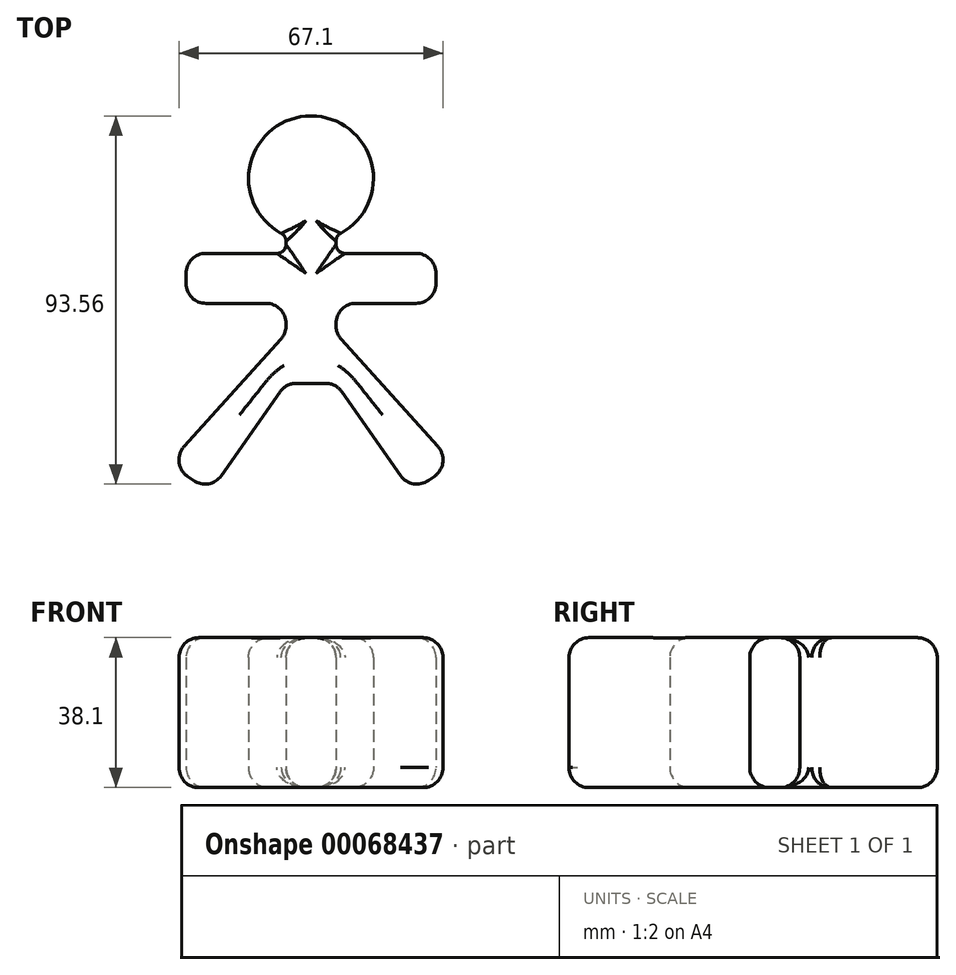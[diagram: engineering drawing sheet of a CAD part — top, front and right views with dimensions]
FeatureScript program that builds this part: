
annotation { "Feature Type Name" : "Feature", "Feature Type Description" : "" }
export const myFeature = defineFeature(function(context is Context, id is Id, definition is map)
    precondition{}
    {
        {
            var Q0;
            Q0=qCreatedBy(makeId("Top.planeOp"),FACE);
            var sketch = newSketch(context, id + "F0", { "sketchPlane" : qUnion([Q0])});
            skLineSegment(sketch, "E0.bottom", {"start": v(0, 0) * mm, "end": v(12.7, 0) * mm});
            skLineSegment(sketch, "E0.top", {"start": v(0, 38.1) * mm, "end": v(12.7, 38.1) * mm});
            skLineSegment(sketch, "E0.left", {"start": v(0, 0) * mm, "end": v(0, 38.1) * mm});
            skLineSegment(sketch, "E0.right", {"start": v(12.7, 0) * mm, "end": v(12.7, 38.1) * mm});
            skLineSegment(sketch, "E1.bottom", {"start": v(-25.4, 33.02) * mm, "end": v(38.1, 33.02) * mm});
            skLineSegment(sketch, "E1.top", {"start": v(-25.4, 20.32) * mm, "end": v(38.1, 20.32) * mm});
            skLineSegment(sketch, "E1.left", {"start": v(-25.4, 33.02) * mm, "end": v(-25.4, 20.32) * mm});
            skLineSegment(sketch, "E1.right", {"start": v(38.1, 33.02) * mm, "end": v(38.1, 20.32) * mm});
            skLineSegment(sketch, "E2.top", {"start": v(-19.33, -27.6) * mm, "end": v(-29.73, -20.32) * mm});
            skLineSegment(sketch, "E2.left", {"start": v(0, 0) * mm, "end": v(-19.33, -27.6) * mm});
            skLineSegment(sketch, "E2.right", {"start": v(0, 12.7) * mm, "end": v(-29.73, -20.32) * mm});
            skLineSegment(sketch, "E3.top", {"start": v(32.03, -27.6) * mm, "end": v(42.43, -20.32) * mm});
            skLineSegment(sketch, "E3.left", {"start": v(12.7, 0) * mm, "end": v(32.03, -27.6) * mm});
            skLineSegment(sketch, "E3.right", {"start": v(12.7, 12.7) * mm, "end": v(42.43, -20.32) * mm});
            skCircle(sketch, "E4", {"center": v(6.35, 52.07) * mm, "radius": 15.88 * mm});
            skSolve(sketch);
        }
        {
            var Q0;
            Q0 = qSketchRegion(id + "F0", true);
            extrude(context, id + "F1", {"entities" : qUnion([Q0]), "depth" : 38.1 * mm});
        }
        {
            var Q0;
            Q0=makeQuery(id+"F1.opExtrude","CAP_FACE",FACE,{"disambiguationData":[OSD([sQuery(id+"F0.wireOp",EDGE,"E0.bottom"),sQuery(id+"F0.wireOp",EDGE,"E0.left"),sQuery(id+"F0.wireOp",EDGE,"E0.right"),sQuery(id+"F0.wireOp",EDGE,"E1.bottom"),sQuery(id+"F0.wireOp",EDGE,"E1.top"),sQuery(id+"F0.wireOp",EDGE,"E1.left"),sQuery(id+"F0.wireOp",EDGE,"E1.right"),sQuery(id+"F0.wireOp",EDGE,"E2.top"),sQuery(id+"F0.wireOp",EDGE,"E2.left"),sQuery(id+"F0.wireOp",EDGE,"E2.right"),sQuery(id+"F0.wireOp",EDGE,"E3.top"),sQuery(id+"F0.wireOp",EDGE,"E3.left"),sQuery(id+"F0.wireOp",EDGE,"E3.right"),sQuery(id+"F0.wireOp",EDGE,"E4")])],"isStart":false});
            var Q1;
            Q1=makeQuery(id+"F1.opExtrude","CAP_FACE",FACE,{"disambiguationData":[OSD([sQuery(id+"F0.wireOp",EDGE,"E0.bottom"),sQuery(id+"F0.wireOp",EDGE,"E0.left"),sQuery(id+"F0.wireOp",EDGE,"E0.right"),sQuery(id+"F0.wireOp",EDGE,"E1.bottom"),sQuery(id+"F0.wireOp",EDGE,"E1.top"),sQuery(id+"F0.wireOp",EDGE,"E1.left"),sQuery(id+"F0.wireOp",EDGE,"E1.right"),sQuery(id+"F0.wireOp",EDGE,"E2.top"),sQuery(id+"F0.wireOp",EDGE,"E2.left"),sQuery(id+"F0.wireOp",EDGE,"E2.right"),sQuery(id+"F0.wireOp",EDGE,"E3.top"),sQuery(id+"F0.wireOp",EDGE,"E3.left"),sQuery(id+"F0.wireOp",EDGE,"E3.right"),sQuery(id+"F0.wireOp",EDGE,"E4")])],"isStart":true});
            var Q2;
            Q2=makeQuery(id+"F1.opExtrude","SWEPT_FACE",FACE,{"disambiguationData":[OSD([sQuery(id+"F0.wireOp",EDGE,"E1.left")])]});
            var Q3;
            {var subQ0=sQuery(id+"F0.wireOp",EDGE,"E0.left");Q3=makeQuery(id+"F1.opExtrude","SWEPT_FACE",FACE,{"disambiguationData":[OSD([subQ0]),TDD([makeQuery(id+"F0.imprint","IMPRINT",EDGE,{"disambiguationData":[TD([[makeQuery(id+"F0.imprint","INTERSECT",VERTEX,{"derivedFrom":[subQ0,sQuery(id+"F0.wireOp",EDGE,"E2.right")]}),-1.0]])],"derivedFrom":subQ0})])]});}
            var Q4;
            Q4=makeQuery(id+"F1.opExtrude","SWEPT_FACE",FACE,{"disambiguationData":[OSD([sQuery(id+"F0.wireOp",EDGE,"E2.top")])]});
            var Q5;
            Q5=makeQuery(id+"F1.opExtrude","SWEPT_FACE",FACE,{"disambiguationData":[OSD([sQuery(id+"F0.wireOp",EDGE,"E0.bottom")])]});
            var Q6;
            Q6=makeQuery(id+"F1.opExtrude","SWEPT_FACE",FACE,{"disambiguationData":[OSD([sQuery(id+"F0.wireOp",EDGE,"E3.top")])]});
            var Q7;
            Q7=makeQuery(id+"F1.opExtrude","SWEPT_FACE",FACE,{"disambiguationData":[OSD([sQuery(id+"F0.wireOp",EDGE,"E1.right")])]});
            var Q8;
            {var subQ0=sQuery(id+"F0.wireOp",EDGE,"E0.right");Q8=makeQuery(id+"F1.opExtrude","SWEPT_FACE",FACE,{"disambiguationData":[OSD([subQ0]),TDD([makeQuery(id+"F0.imprint","IMPRINT",EDGE,{"disambiguationData":[TD([[makeQuery(id+"F0.imprint","INTERSECT",VERTEX,{"derivedFrom":[subQ0,sQuery(id+"F0.wireOp",EDGE,"E3.right")]}),-1.0]])],"derivedFrom":subQ0})])]});}
            fillet(context, id + "F2", {"entities" : qUnion([Q0, Q1, Q2, Q3, Q4, Q5, Q6, Q7, Q8]), "radius" : 5.08 * mm, "tangentPropagation" : true, "allowEdgeOverflow" : false});
        }
        {
            var Q0;
            {var subQ0=sQuery(id+"F0.wireOp",EDGE,"E0.left");Q0=makeQuery(id+"F1.opExtrude","SWEPT_FACE",FACE,{"disambiguationData":[OSD([subQ0]),TDD([makeQuery(id+"F0.imprint","IMPRINT",EDGE,{"disambiguationData":[TD([[makeQuery(id+"F0.imprint","INTERSECT",VERTEX,{"derivedFrom":[subQ0,sQuery(id+"F0.wireOp",EDGE,"E1.bottom")]}),-1.0]])],"derivedFrom":subQ0})])]});}
            var Q1;
            {var subQ0=sQuery(id+"F0.wireOp",EDGE,"E0.right");Q1=makeQuery(id+"F1.opExtrude","SWEPT_FACE",FACE,{"disambiguationData":[OSD([subQ0]),TDD([makeQuery(id+"F0.imprint","IMPRINT",EDGE,{"disambiguationData":[TD([[makeQuery(id+"F0.imprint","INTERSECT",VERTEX,{"derivedFrom":[subQ0,sQuery(id+"F0.wireOp",EDGE,"E1.bottom")]}),-1.0]])],"derivedFrom":subQ0})])]});}
            fillet(context, id + "F3", {"entities" : qUnion([Q0, Q1]), "radius" : 2.3 * mm, "tangentPropagation" : true, "allowEdgeOverflow" : false});
        }
    });
